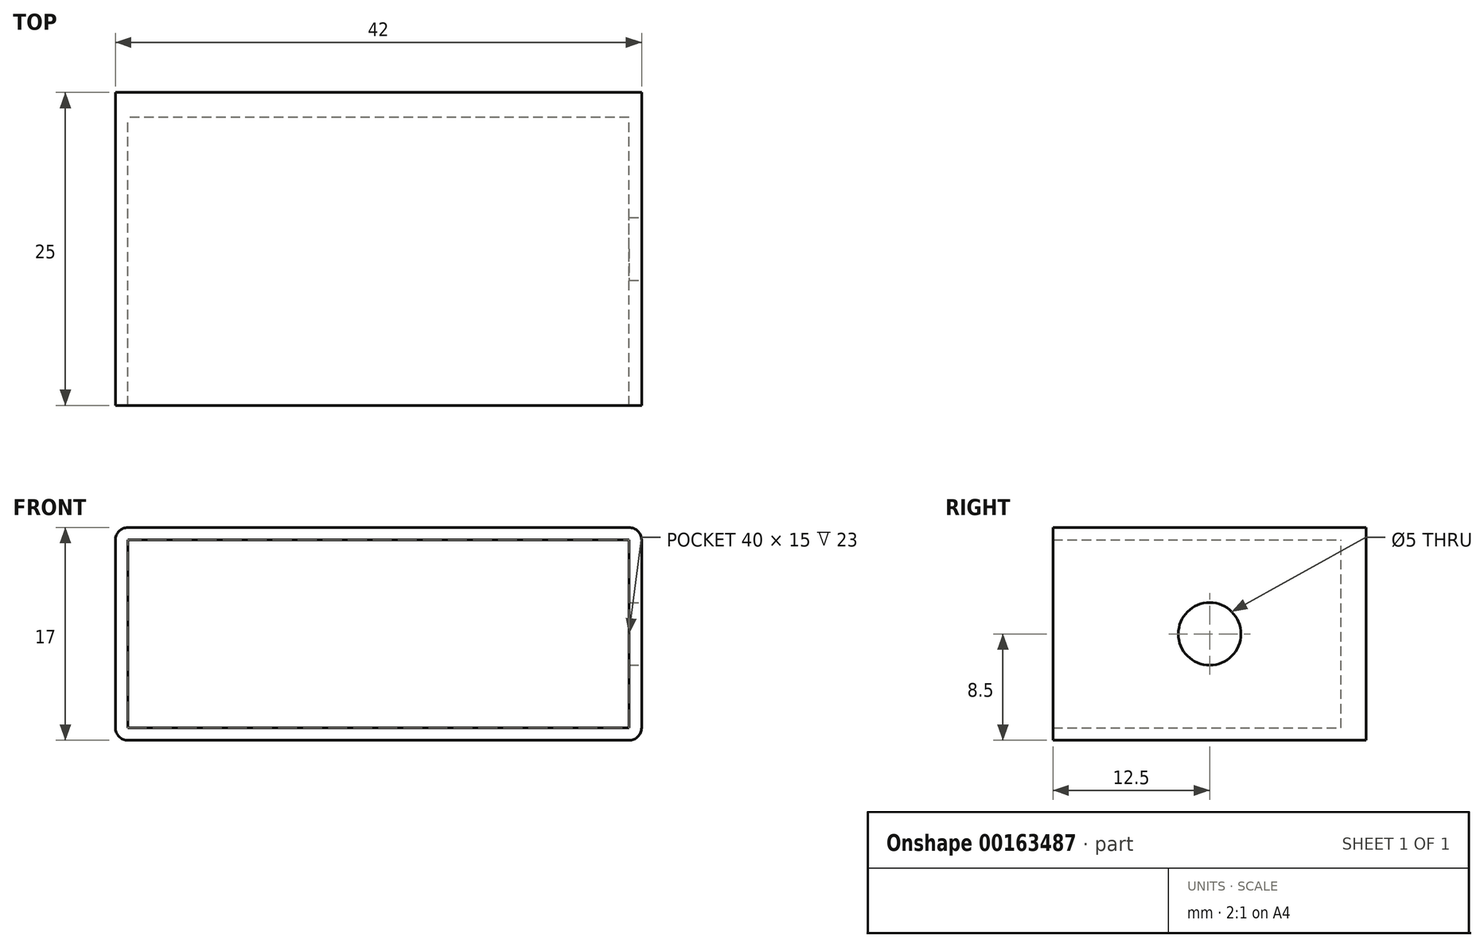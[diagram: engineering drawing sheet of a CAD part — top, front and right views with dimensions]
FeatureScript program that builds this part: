
annotation { "Feature Type Name" : "Feature", "Feature Type Description" : "" }
export const myFeature = defineFeature(function(context is Context, id is Id, definition is map)
    precondition{}
    {
        {
            var Q0;
            Q0=qCreatedBy(makeId("Front.planeOp"),FACE);
            var sketch = newSketch(context, id + "F0", { "sketchPlane" : qUnion([Q0])});
            skLineSegment(sketch, "E0.bottom", {"start": v(20, -7.5) * mm, "end": v(-20, -7.5) * mm});
            skLineSegment(sketch, "E0.top", {"start": v(20, 7.5) * mm, "end": v(-20, 7.5) * mm});
            skLineSegment(sketch, "E0.left", {"start": v(20, -7.5) * mm, "end": v(20, 7.5) * mm});
            skLineSegment(sketch, "E0.right", {"start": v(-20, -7.5) * mm, "end": v(-20, 7.5) * mm});
            skPoint(sketch, "E0.middle", {"position": v(0, 0) * mm});
            skLineSegment(sketch, "E1.bottom", {"start": v(20, -8.5) * mm, "end": v(-20, -8.5) * mm});
            skLineSegment(sketch, "E1.top", {"start": v(20, 8.5) * mm, "end": v(-20, 8.5) * mm});
            skLineSegment(sketch, "E1.left", {"start": v(21, -7.5) * mm, "end": v(21, 7.5) * mm});
            skLineSegment(sketch, "E1.right", {"start": v(-21, -7.5) * mm, "end": v(-21, 7.5) * mm});
            skPoint(sketch, "E2.visualSharp", {"position": v(-21, 8.5) * mm});
            skArc(sketch, "E2.filletArc", {"start": v(-20, 8.5) * mm, "mid": v(-20.7, 8.2) * mm, "end": v(-21, 7.5) * mm});
            skPoint(sketch, "E3.visualSharp", {"position": v(-21, -8.5) * mm});
            skArc(sketch, "E3.filletArc", {"start": v(-21, -7.5) * mm, "mid": v(-20.7, -8.2) * mm, "end": v(-20, -8.5) * mm});
            skPoint(sketch, "E4.visualSharp", {"position": v(21, -8.5) * mm});
            skArc(sketch, "E4.filletArc", {"start": v(20, -8.5) * mm, "mid": v(20.7, -8.2) * mm, "end": v(21, -7.5) * mm});
            skPoint(sketch, "E5.visualSharp", {"position": v(21, 8.5) * mm});
            skArc(sketch, "E5.filletArc", {"start": v(21, 7.5) * mm, "mid": v(20.7, 8.2) * mm, "end": v(20, 8.5) * mm});
            skSolve(sketch);
        }
        {
            var Q0;
            Q0=makeQuery(id+"F0.imprint","IMPRINT",FACE,{"disambiguationData":[TD([[makeQuery(id+"F0.imprint","IMPRINT",EDGE,{"derivedFrom":sQuery(id+"F0.wireOp",EDGE,"E0.bottom")}),1.0]])]});
            extrude(context, id + "F1", {"entities" : qUnion([Q0]), "depth" : 25 * mm});
        }
        {
            var Q0;
            Q0=makeQuery(id+"F0.imprint","IMPRINT",FACE,{"disambiguationData":[TD([[makeQuery(id+"F0.imprint","IMPRINT",EDGE,{"derivedFrom":sQuery(id+"F0.wireOp",EDGE,"E0.bottom")}),-1.0]])]});
            extrude(context, id + "F2", {"entities" : qUnion([Q0]), "operationType" : NewBodyOperationType.ADD, "depth" : 2 * mm});
        }
        {
            var Q0;
            Q0=makeQuery(id+"F1.opExtrude","SWEPT_FACE",FACE,{"disambiguationData":[OSD([sQuery(id+"F0.wireOp",EDGE,"E1.left")])]});
            var sketch = newSketch(context, id + "F3", { "sketchPlane" : qUnion([Q0])});
            skCircle(sketch, "E6", {"center": v(-12.5, 0) * mm, "radius": 2.5 * mm});
            skPoint(sketch, "E6.centerSnap0", {"position": v(-12.5, 7.5) * mm});
            skSolve(sketch);
        }
        {
            var Q0;
            Q0=makeQuery(id+"F3.imprint","IMPRINT",FACE,{"disambiguationData":[TD([[makeQuery(id+"F3.imprint","IMPRINT",EDGE,{"derivedFrom":sQuery(id+"F3.wireOp",EDGE,"E6")}),1.0]])]});
            extrude(context, id + "F4", {"entities" : qUnion([Q0]), "operationType" : NewBodyOperationType.REMOVE, "oppositeDirection" : true, "depth" : 5 * mm});
        }
    });
